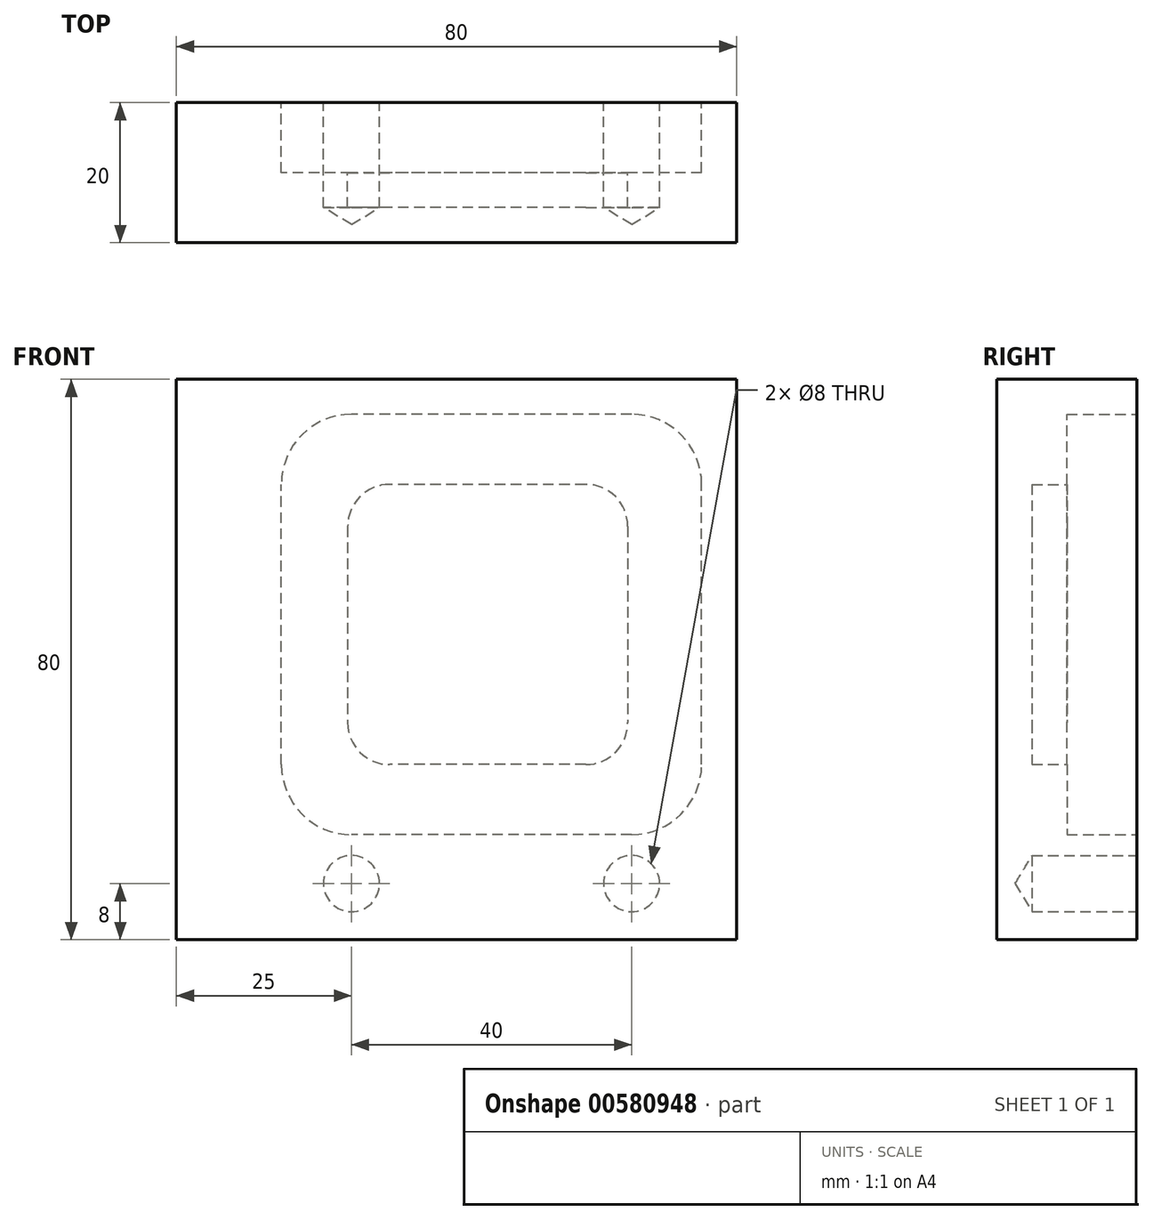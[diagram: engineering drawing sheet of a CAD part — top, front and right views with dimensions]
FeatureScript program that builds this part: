
annotation { "Feature Type Name" : "Feature", "Feature Type Description" : "" }
export const myFeature = defineFeature(function(context is Context, id is Id, definition is map)
    precondition{}
    {
        {
            var Q0;
            Q0=qCreatedBy(makeId("Front.planeOp"),FACE);
            var sketch = newSketch(context, id + "F0", { "sketchPlane" : qUnion([Q0])});
            skLineSegment(sketch, "E0.bottom", {"start": v(40, -40) * mm, "end": v(-40, -40) * mm});
            skLineSegment(sketch, "E0.top", {"start": v(40, 40) * mm, "end": v(-40, 40) * mm});
            skLineSegment(sketch, "E0.left", {"start": v(40, -40) * mm, "end": v(40, 40) * mm});
            skLineSegment(sketch, "E0.right", {"start": v(-40, -40) * mm, "end": v(-40, 40) * mm});
            skLineSegment(sketch, "E1", {"start": v(0, -40) * mm, "end": v(0, 0) * mm, "construction": true});
            skLineSegment(sketch, "E2", {"start": v(0, 0) * mm, "end": v(40, 0) * mm, "construction": true});
            skSolve(sketch);
        }
        {
            var Q0;
            Q0=makeQuery(id+"F0.imprint","IMPRINT",FACE,{"disambiguationData":[TD([[makeQuery(id+"F0.imprint","IMPRINT",EDGE,{"derivedFrom":sQuery(id+"F0.wireOp",EDGE,"E0.bottom")}),-1.0]])]});
            extrude(context, id + "F1", {"entities" : qUnion([Q0]), "depth" : 20 * mm, "offsetDistance" : 25 * mm});
        }
        {
            var Q0;
            Q0=makeQuery(id+"F1.opExtrude","CAP_FACE",FACE,{"disambiguationData":[OSD([sQuery(id+"F0.wireOp",EDGE,"E0.bottom"),sQuery(id+"F0.wireOp",EDGE,"E0.top"),sQuery(id+"F0.wireOp",EDGE,"E0.left"),sQuery(id+"F0.wireOp",EDGE,"E0.right")])],"isStart":true});
            var sketch = newSketch(context, id + "F2", { "sketchPlane" : qUnion([Q0])});
            skCircle(sketch, "E3", {"center": v(-25, -32) * mm, "radius": 4 * mm});
            skCircle(sketch, "E4", {"center": v(15, -32) * mm, "radius": 4 * mm});
            skLineSegment(sketch, "E5.bottom", {"start": v(-25, -25) * mm, "end": v(15, -25) * mm});
            skLineSegment(sketch, "E5.left", {"start": v(-35, -15) * mm, "end": v(-35, 25) * mm});
            skLineSegment(sketch, "E5.right", {"start": v(25, -15) * mm, "end": v(25, 25) * mm});
            skArc(sketch, "E6", {"start": v(-35, -15) * mm, "mid": v(-32.07, -22.07) * mm, "end": v(-25, -25) * mm});
            skArc(sketch, "E7", {"start": v(-25, 35) * mm, "mid": v(-32.07, 32.07) * mm, "end": v(-35, 25) * mm});
            skArc(sketch, "E8", {"start": v(25, 25) * mm, "mid": v(22.07, 32.07) * mm, "end": v(15, 35) * mm});
            skArc(sketch, "E9", {"start": v(15, -25) * mm, "mid": v(22.07, -22.07) * mm, "end": v(25, -15) * mm});
            skLineSegment(sketch, "E10", {"start": v(-18.46, 25) * mm, "end": v(9.54, 25) * mm});
            skLineSegment(sketch, "E11", {"start": v(-25, 35) * mm, "end": v(15, 35) * mm});
            skLineSegment(sketch, "E12", {"start": v(-18.46, -15) * mm, "end": v(9.54, -15) * mm});
            skArc(sketch, "E13", {"start": v(-18.46, 25) * mm, "mid": v(-22.7, 23.24) * mm, "end": v(-24.46, 19) * mm});
            skArc(sketch, "E14", {"start": v(15.54, 19) * mm, "mid": v(13.78, 23.24) * mm, "end": v(9.54, 25) * mm});
            skLineSegment(sketch, "E15", {"start": v(15.54, 19) * mm, "end": v(15.54, -9) * mm});
            skLineSegment(sketch, "E16", {"start": v(-24.46, 19) * mm, "end": v(-24.46, -9) * mm});
            skArc(sketch, "E17", {"start": v(-24.46, -9) * mm, "mid": v(-22.7, -13.24) * mm, "end": v(-18.46, -15) * mm});
            skArc(sketch, "E18", {"start": v(9.54, -15) * mm, "mid": v(13.78, -13.24) * mm, "end": v(15.54, -9) * mm});
            skSolve(sketch);
        }
        {
            var Q0;
            Q0=sQuery(id+"F2.wireOp",VERTEX,"E3.center");
            var Q1;
            Q1=sQuery(id+"F2.wireOp",VERTEX,"E4.center");
            var Q2;
            Q2=makeQuery(id+"F1.opExtrude","SWEPT_BODY",BODY,{"disambiguationData":[OSD([sQuery(id+"F0.wireOp",EDGE,"E0.bottom"),sQuery(id+"F0.wireOp",EDGE,"E0.top"),sQuery(id+"F0.wireOp",EDGE,"E0.left"),sQuery(id+"F0.wireOp",EDGE,"E0.right")])]});
            hole(context, id + "F3", {"style" : HoleStyle.SIMPLE, "endStyle" : HoleEndStyle.BLIND, "holeDiameter" : 8 * mm, "majorDiameter" : 5 * mm, "holeDepth" : 15 * mm, "isTappedThrough" : true, "tappedDepth" : 12 * mm, "tapClearance" : 3, "locations" : qUnion([Q0, Q1]), "scope" : qUnion([Q2])});
        }
        {
            var Q0;
            Q0=makeQuery(id+"F2.imprint","IMPRINT",FACE,{"disambiguationData":[TD([[makeQuery(id+"F2.imprint","IMPRINT",EDGE,{"derivedFrom":sQuery(id+"F2.wireOp",EDGE,"E5.bottom")}),1.0]])]});
            extrude(context, id + "F4", {"entities" : qUnion([Q0]), "operationType" : NewBodyOperationType.REMOVE, "oppositeDirection" : true, "depth" : 10 * mm, "offsetDistance" : 25 * mm});
        }
        {
            var Q0;
            Q0=makeQuery(id+"F2.imprint","IMPRINT",FACE,{"disambiguationData":[TD([[makeQuery(id+"F2.imprint","IMPRINT",EDGE,{"derivedFrom":sQuery(id+"F2.wireOp",EDGE,"E10")}),-1.0]])]});
            extrude(context, id + "F5", {"entities" : qUnion([Q0]), "operationType" : NewBodyOperationType.REMOVE, "oppositeDirection" : true, "depth" : 15 * mm, "offsetDistance" : 25 * mm});
        }
    });
